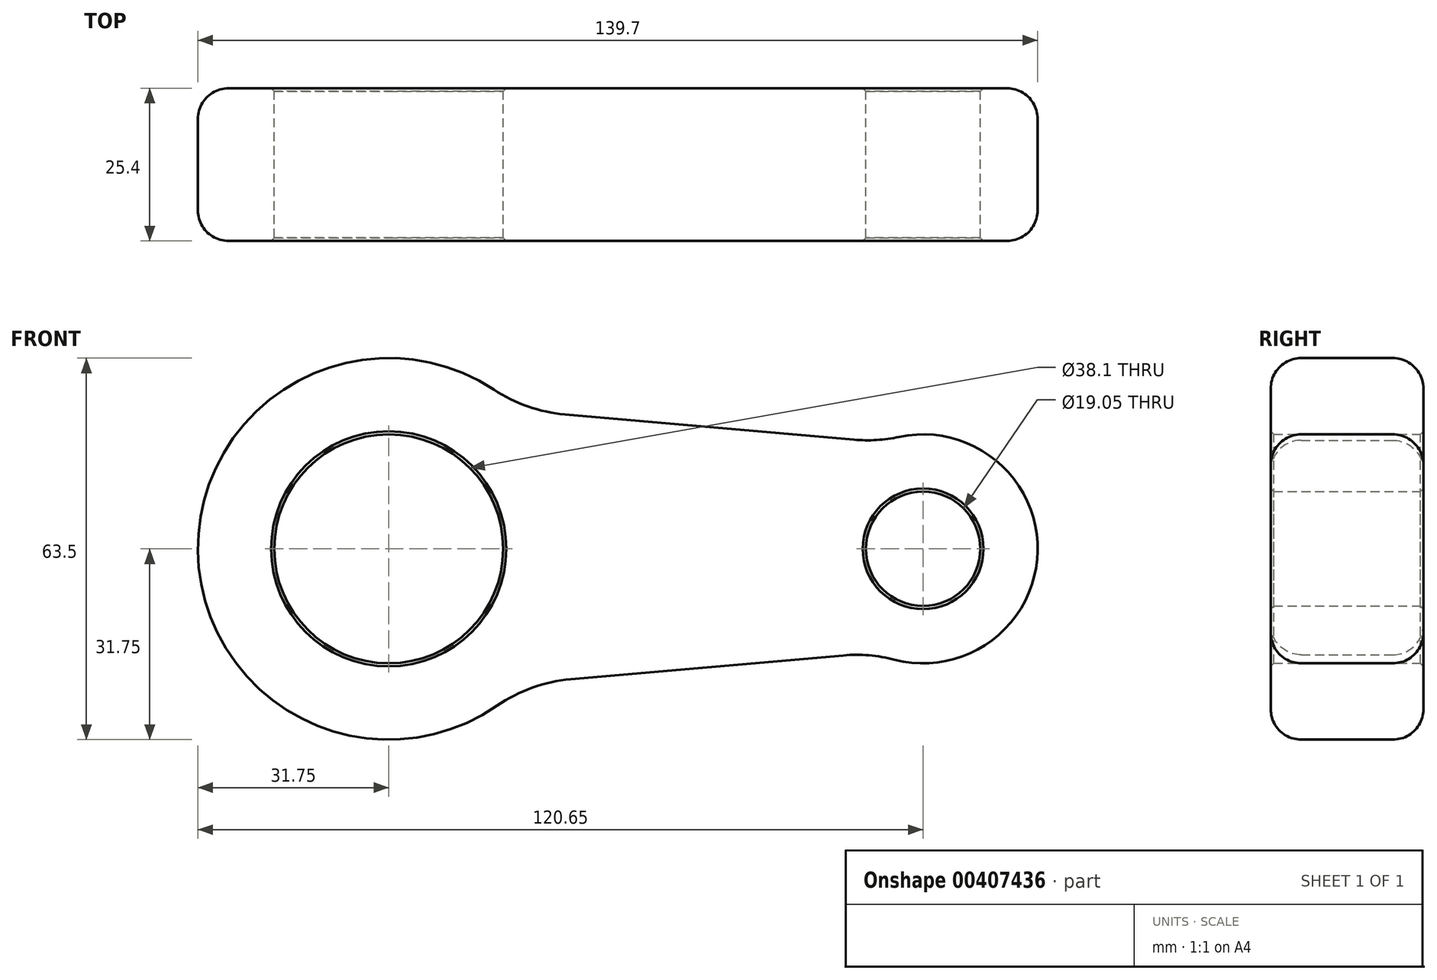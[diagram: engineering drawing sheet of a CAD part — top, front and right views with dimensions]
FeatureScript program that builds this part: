
annotation { "Feature Type Name" : "Feature", "Feature Type Description" : "" }
export const myFeature = defineFeature(function(context is Context, id is Id, definition is map)
    precondition{}
    {
        {
            var Q0;
            Q0=qCreatedBy(makeId("Front.planeOp"),FACE);
            var sketch = newSketch(context, id + "F0", { "sketchPlane" : qUnion([Q0])});
            skArc(sketch, "E0", {"start": v(17.51, 26.48) * mm, "mid": v(-31.75, -0.33) * mm, "end": v(18.05, -26.12) * mm});
            skArc(sketch, "E1", {"start": v(84.15, -18.45) * mm, "mid": v(107.95, -0.4) * mm, "end": v(84.91, 18.63) * mm});
            skLineSegment(sketch, "E2", {"start": v(29.3, 22.37) * mm, "end": v(77.38, 18.16) * mm});
            skLineSegment(sketch, "E3", {"start": v(75.6, -17.74) * mm, "end": v(30.28, -21.7) * mm});
            skPoint(sketch, "E4.visualSharp", {"position": v(21.87, 23.02) * mm});
            skArc(sketch, "E4.filletArc", {"start": v(17.51, 26.48) * mm, "mid": v(23.15, 23.69) * mm, "end": v(29.3, 22.37) * mm});
            skPoint(sketch, "E5.visualSharp", {"position": v(82, 17.76) * mm});
            skArc(sketch, "E5.filletArc", {"start": v(77.38, 18.16) * mm, "mid": v(81.17, 18.11) * mm, "end": v(84.91, 18.63) * mm});
            skPoint(sketch, "E6.visualSharp", {"position": v(80.88, -17.28) * mm});
            skArc(sketch, "E6.filletArc", {"start": v(84.15, -18.45) * mm, "mid": v(79.9, -17.73) * mm, "end": v(75.6, -17.74) * mm});
            skPoint(sketch, "E7.visualSharp", {"position": v(22.51, -22.39) * mm});
            skArc(sketch, "E7.filletArc", {"start": v(30.28, -21.7) * mm, "mid": v(23.88, -23.12) * mm, "end": v(18.05, -26.12) * mm});
            skLineSegment(sketch, "E8", {"start": v(0, 0) * mm, "end": v(88.9, 0) * mm, "construction": true});
            skCircle(sketch, "E9", {"center": v(0, 0) * mm, "radius": 19.05 * mm});
            skCircle(sketch, "E10", {"center": v(88.9, 0) * mm, "radius": 9.53 * mm});
            skSolve(sketch);
        }
        {
            var Q0;
            Q0=makeQuery(id+"F0.imprint","IMPRINT",FACE,{"disambiguationData":[TD([[makeQuery(id+"F0.imprint","IMPRINT",EDGE,{"derivedFrom":sQuery(id+"F0.wireOp",EDGE,"E0")}),1.0]])]});
            extrude(context, id + "F1", {"entities" : qUnion([Q0]), "endBound" : BoundingType.SYMMETRIC, "depth" : 25.4 * mm});
        }
        {
            var Q0;
            Q0=makeQuery(id+"F1.opExtrude","CAP_EDGE",EDGE,{"disambiguationData":[OSD([sQuery(id+"F0.wireOp",EDGE,"E0")])],"isStart":false});
            var Q1;
            Q1=makeQuery(id+"F1.opExtrude","CAP_EDGE",EDGE,{"disambiguationData":[OSD([sQuery(id+"F0.wireOp",EDGE,"E0")])],"isStart":true});
            fillet(context, id + "F2", {"entities" : qUnion([Q0, Q1]), "radius" : 5.08 * mm, "tangentPropagation" : true, "allowEdgeOverflow" : false});
        }
        {
            var Q0;
            Q0=makeQuery(id+"F1.opExtrude","CAP_EDGE",EDGE,{"disambiguationData":[OSD([sQuery(id+"F0.wireOp",EDGE,"E9")])],"isStart":false});
            var Q1;
            Q1=makeQuery(id+"F1.opExtrude","CAP_EDGE",EDGE,{"disambiguationData":[OSD([sQuery(id+"F0.wireOp",EDGE,"E10")])],"isStart":false});
            var Q2;
            Q2=makeQuery(id+"F1.opExtrude","CAP_EDGE",EDGE,{"disambiguationData":[OSD([sQuery(id+"F0.wireOp",EDGE,"E9")])],"isStart":true});
            var Q3;
            Q3=makeQuery(id+"F1.opExtrude","CAP_EDGE",EDGE,{"disambiguationData":[OSD([sQuery(id+"F0.wireOp",EDGE,"E10")])],"isStart":true});
            chamfer(context, id + "F3", {"entities" : qUnion([Q0, Q1, Q2, Q3]), "width" : 0.5 * mm, "tangentPropagation" : true});
        }
    });
